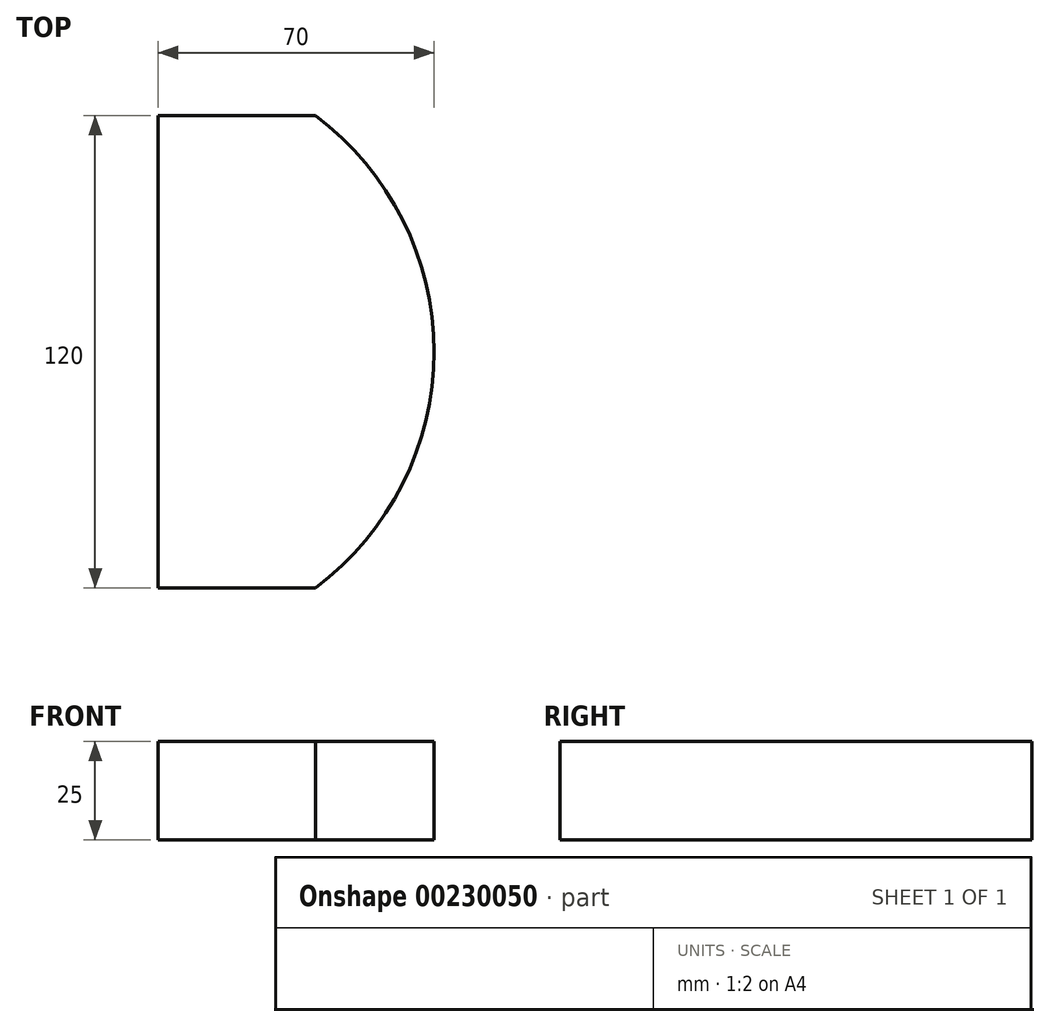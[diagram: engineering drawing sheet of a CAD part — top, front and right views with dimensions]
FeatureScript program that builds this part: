
annotation { "Feature Type Name" : "Feature", "Feature Type Description" : "" }
export const myFeature = defineFeature(function(context is Context, id is Id, definition is map)
    precondition{}
    {
        {
            var Q0;
            Q0=qCreatedBy(makeId("Top.planeOp"),FACE);
            var sketch = newSketch(context, id + "F0", { "sketchPlane" : qUnion([Q0])});
            skLineSegment(sketch, "E0.bottom", {"start": v(17.2, -18.23) * mm, "end": v(-22.8, -18.23) * mm});
            skLineSegment(sketch, "E0.top", {"start": v(17.2, 101.77) * mm, "end": v(-22.8, 101.77) * mm});
            skLineSegment(sketch, "E0.left", {"start": v(17.2, -18.23) * mm, "end": v(17.2, 101.77) * mm});
            skLineSegment(sketch, "E0.right", {"start": v(-22.8, -18.23) * mm, "end": v(-22.8, 101.77) * mm});
            skArc(sketch, "E1", {"start": v(17.2, -18.23) * mm, "mid": v(47.2, 41.77) * mm, "end": v(17.2, 101.77) * mm});
            skSolve(sketch);
        }
        {
            var Q0;
            Q0 = qSketchRegion(id + "F0", true);
            extrude(context, id + "F1", {"entities" : qUnion([Q0]), "depth" : 25 * mm});
        }
    });
